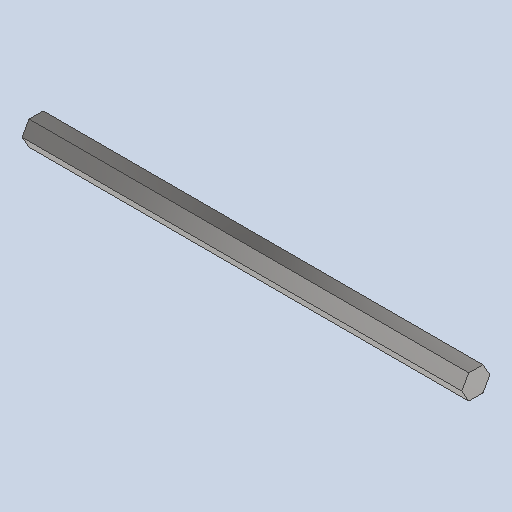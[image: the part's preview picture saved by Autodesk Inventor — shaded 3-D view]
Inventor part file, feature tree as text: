
AUTODESK INVENTOR PART (.ipt)
format: ipt  version: 2023 (Build 270158000, 158)  size: 92,160 bytes
history: native  units: in
note: dims shown in document units (in); Inventor stores cm internally (conversion verified against a paired STEP export)
features: other x3, sketch x1
ambient origin geometry x8: Origin, YZ Plane, XZ Plane, XY Plane, X Axis, Y Axis, Z Axis, Center Point
bodies: Solid1 (feature_tree)
feature tree (4):
  other  "9in-0.5inHexAxel.ipt"
  other  "Solid1::9in-0.5inHexAxel.ipt"
  other  "TaggingFeature1"
  sketch  "Sketch1"  dims[d0=0.3937in]
